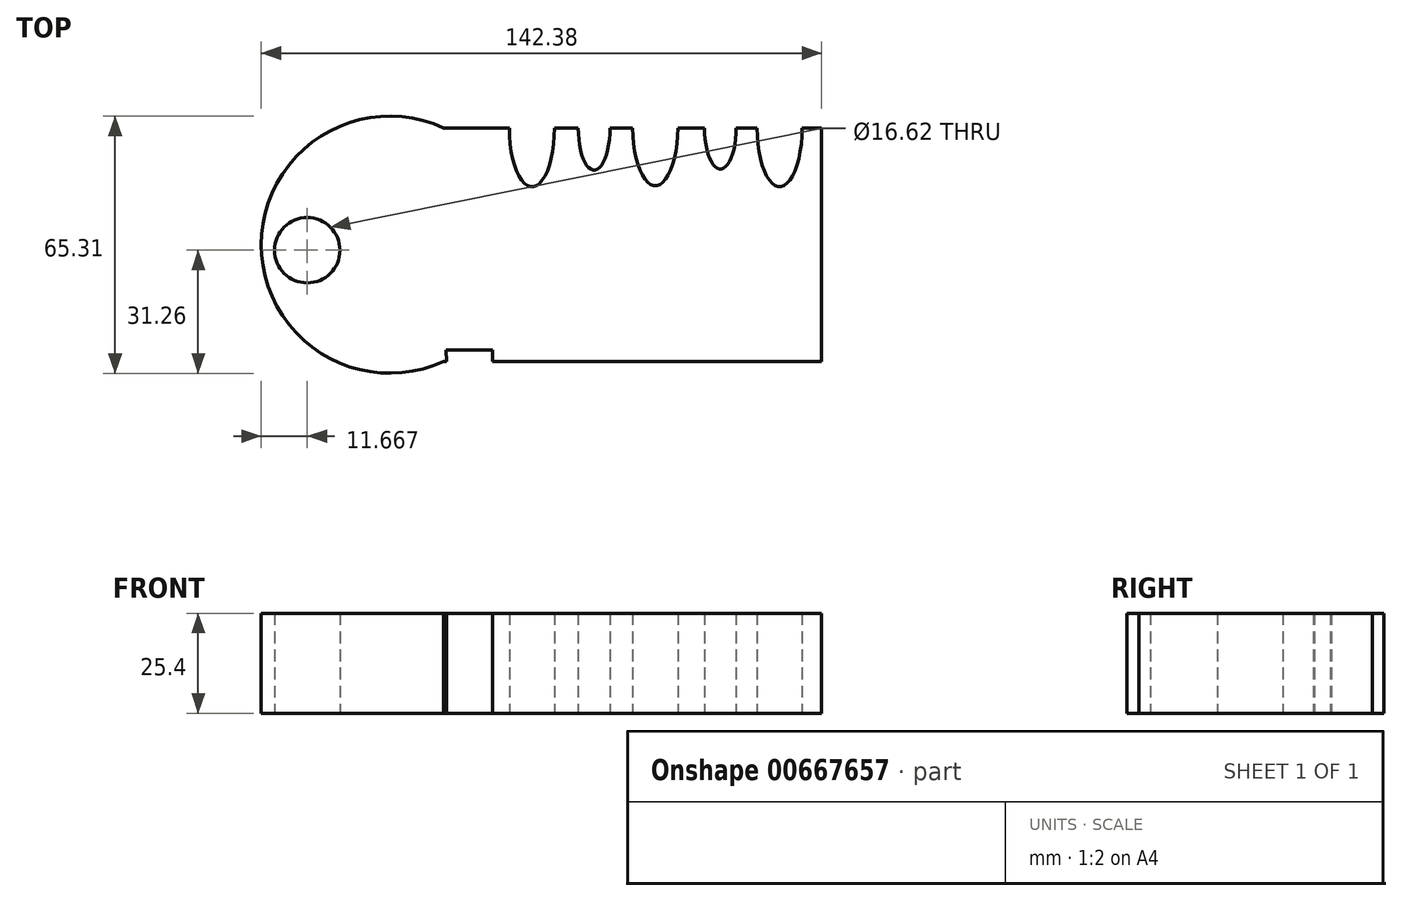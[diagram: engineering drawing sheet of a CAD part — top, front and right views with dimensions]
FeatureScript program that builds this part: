
annotation { "Feature Type Name" : "Feature", "Feature Type Description" : "" }
export const myFeature = defineFeature(function(context is Context, id is Id, definition is map)
    precondition{}
    {
        {
            var Q0;
            Q0=qCreatedBy(makeId("Top.planeOp"),FACE);
            var sketch = newSketch(context, id + "F0", { "sketchPlane" : qUnion([Q0])});
            skLineSegment(sketch, "E0.bottom", {"start": v(-24.54, 31.05) * mm, "end": v(71.52, 31.05) * mm});
            skLineSegment(sketch, "E0.top", {"start": v(-24.54, -28.26) * mm, "end": v(71.52, -28.26) * mm});
            skLineSegment(sketch, "E0.left", {"start": v(-24.54, 31.05) * mm, "end": v(-24.54, -28.26) * mm});
            skLineSegment(sketch, "E0.right", {"start": v(71.52, 31.05) * mm, "end": v(71.52, -28.26) * mm});
            skArc(sketch, "E1", {"start": v(-24.54, 31.05) * mm, "mid": v(-70.86, 1.4) * mm, "end": v(-24.54, -28.26) * mm});
            skSolve(sketch);
        }
        {
            var Q0;
            Q0=makeQuery(id+"F0.imprint","IMPRINT",FACE,{"disambiguationData":[TD([[makeQuery(id+"F0.imprint","IMPRINT",EDGE,{"derivedFrom":sQuery(id+"F0.wireOp",EDGE,"E0.bottom")}),-1.0]])]});
            var Q1;
            Q1=makeQuery(id+"F0.imprint","IMPRINT",FACE,{"disambiguationData":[TD([[makeQuery(id+"F0.imprint","IMPRINT",EDGE,{"derivedFrom":sQuery(id+"F0.wireOp",EDGE,"E0.left")}),-1.0]])]});
            extrude(context, id + "F1", {"entities" : qUnion([Q0, Q1]), "depth" : 25.4 * mm, "offsetDistance" : 25.4 * mm});
        }
        {
            var Q0;
            Q0=qCreatedBy(makeId("Top.planeOp"),FACE);
            var sketch = newSketch(context, id + "F2", { "sketchPlane" : qUnion([Q0])});
            skCircle(sketch, "E2", {"center": v(-53.84, 0) * mm, "radius": 6.97 * mm});
            skSolve(sketch);
        }
        {
            var Q0;
            Q0=makeQuery(id+"F2.imprint","IMPRINT",FACE,{"disambiguationData":[TD([[makeQuery(id+"F2.imprint","IMPRINT",EDGE,{"derivedFrom":sQuery(id+"F2.wireOp",EDGE,"E2")}),1.0]])]});
            extrude(context, id + "F3", {"entities" : qUnion([Q0]), "operationType" : NewBodyOperationType.ADD, "depth" : 25.4 * mm, "offsetDistance" : 25.4 * mm});
        }
        {
            var Q0;
            Q0=qCreatedBy(makeId("Top.planeOp"),FACE);
            var sketch = newSketch(context, id + "F4", { "sketchPlane" : qUnion([Q0])});
            skCircle(sketch, "E3", {"center": v(-59.2, 0) * mm, "radius": 8.3 * mm});
            skSolve(sketch);
        }
        {
            var Q0;
            Q0=makeQuery(id+"F4.imprint","IMPRINT",FACE,{"disambiguationData":[TD([[makeQuery(id+"F4.imprint","IMPRINT",EDGE,{"derivedFrom":sQuery(id+"F4.wireOp",EDGE,"E3")}),1.0]])]});
            extrude(context, id + "F5", {"entities" : qUnion([Q0]), "operationType" : NewBodyOperationType.REMOVE, "depth" : 43.69 * mm, "offsetDistance" : 25.4 * mm});
        }
        {
            var Q0;
            Q0=qCreatedBy(makeId("Top.planeOp"),FACE);
            var sketch = newSketch(context, id + "F6", { "sketchPlane" : qUnion([Q0])});
            skEllipse(sketch, "E4", {"center": v(-2.1, 31.14) * mm, "majorRadius": 15.05 * mm, "minorRadius": 5.74 * mm, "majorAxis": v(0, 1)});
            skEllipse(sketch, "E5", {"center": v(13.69, 30.9) * mm, "majorRadius": 10.54 * mm, "minorRadius": 4.02 * mm, "majorAxis": v(0, 1)});
            skEllipse(sketch, "E6", {"center": v(29.23, 31.44) * mm, "majorRadius": 15.05 * mm, "minorRadius": 5.74 * mm, "majorAxis": v(0, 1)});
            skEllipse(sketch, "E7", {"center": v(45.78, 31.2) * mm, "majorRadius": 10.54 * mm, "minorRadius": 4.02 * mm, "majorAxis": v(0, 1)});
            skEllipse(sketch, "E8", {"center": v(60.82, 31.23) * mm, "majorRadius": 15.05 * mm, "minorRadius": 5.74 * mm, "majorAxis": v(0, 1)});
            skSolve(sketch);
        }
        {
            var Q0;
            Q0=makeQuery(id+"F6.imprint","IMPRINT",FACE,{"disambiguationData":[TD([[makeQuery(id+"F6.imprint","IMPRINT",EDGE,{"derivedFrom":sQuery(id+"F6.wireOp",EDGE,"E4")}),1.0]])]});
            var Q1;
            Q1=makeQuery(id+"F6.imprint","IMPRINT",FACE,{"disambiguationData":[TD([[makeQuery(id+"F6.imprint","IMPRINT",EDGE,{"derivedFrom":sQuery(id+"F6.wireOp",EDGE,"E5")}),1.0]])]});
            var Q2;
            Q2=makeQuery(id+"F6.imprint","IMPRINT",FACE,{"disambiguationData":[TD([[makeQuery(id+"F6.imprint","IMPRINT",EDGE,{"derivedFrom":sQuery(id+"F6.wireOp",EDGE,"E6")}),1.0]])]});
            var Q3;
            Q3=makeQuery(id+"F6.imprint","IMPRINT",FACE,{"disambiguationData":[TD([[makeQuery(id+"F6.imprint","IMPRINT",EDGE,{"derivedFrom":sQuery(id+"F6.wireOp",EDGE,"E7")}),1.0]])]});
            var Q4;
            Q4=makeQuery(id+"F6.imprint","IMPRINT",FACE,{"disambiguationData":[TD([[makeQuery(id+"F6.imprint","IMPRINT",EDGE,{"derivedFrom":sQuery(id+"F6.wireOp",EDGE,"E8")}),1.0]])]});
            extrude(context, id + "F7", {"entities" : qUnion([Q0, Q1, Q2, Q3, Q4]), "operationType" : NewBodyOperationType.REMOVE, "depth" : 28.7 * mm, "offsetDistance" : 25.4 * mm});
        }
        {
            var Q0;
            Q0=qCreatedBy(makeId("Top.planeOp"),FACE);
            var sketch = newSketch(context, id + "F8", { "sketchPlane" : qUnion([Q0])});
            skLineSegment(sketch, "E9", {"start": v(-17.4, -22.29) * mm, "end": v(71.75, -22.29) * mm});
            skLineSegment(sketch, "E10", {"start": v(-17.4, -22.29) * mm, "end": v(-17.4, -27.3) * mm});
            skLineSegment(sketch, "E11", {"start": v(-17.4, -27.3) * mm, "end": v(-24.17, -27.3) * mm});
            skLineSegment(sketch, "E12", {"start": v(-24.17, -27.3) * mm, "end": v(-27.17, -29.3) * mm});
            skLineSegment(sketch, "E13", {"start": v(71.75, -33.56) * mm, "end": v(71.75, -22.29) * mm});
            skLineSegment(sketch, "E14", {"start": v(71.75, -33.56) * mm, "end": v(-17.4, -33.56) * mm});
            skLineSegment(sketch, "E15", {"start": v(-17.4, -22.29) * mm, "end": v(-17.4, -33.56) * mm});
            skSolve(sketch);
        }
        {
            var Q0;
            {var subQ1=sQuery(id+"F8.wireOp",EDGE,"E9");Q0=makeQuery(id+"F8.imprint","IMPRINT",FACE,{"disambiguationData":[TD([[makeQuery(id+"F8.imprint","IMPRINT",EDGE,{"derivedFrom":subQ1}),-1.0]])]});}
            extrude(context, id + "F9", {"entities" : qUnion([Q0]), "operationType" : NewBodyOperationType.REMOVE, "oppositeDirection" : true, "depth" : 25.4 * mm, "offsetDistance" : 25.4 * mm});
        }
        {
            var Q0;
            Q0=qCreatedBy(makeId("Top.planeOp"),FACE);
            var sketch = newSketch(context, id + "F10", { "sketchPlane" : qUnion([Q0])});
            skLineSegment(sketch, "E16", {"start": v(-23.66, -28.55) * mm, "end": v(-23.66, -35.56) * mm});
            skLineSegment(sketch, "E17", {"start": v(-23.66, -35.56) * mm, "end": v(-12.15, -35.56) * mm});
            skLineSegment(sketch, "E18", {"start": v(-12.15, -35.56) * mm, "end": v(-12.15, -25.3) * mm});
            skLineSegment(sketch, "E19", {"start": v(-12.15, -25.3) * mm, "end": v(-23.92, -25.3) * mm});
            skLineSegment(sketch, "E20", {"start": v(-23.92, -25.3) * mm, "end": v(-23.66, -35.56) * mm});
            skSolve(sketch);
        }
        {
            var Q0;
            Q0=makeQuery(id+"F10.imprint","IMPRINT",FACE,{"disambiguationData":[TD([[makeQuery(id+"F10.imprint","IMPRINT",EDGE,{"derivedFrom":sQuery(id+"F10.wireOp",EDGE,"E17")}),1.0]])]});
            extrude(context, id + "F11", {"entities" : qUnion([Q0]), "operationType" : NewBodyOperationType.REMOVE, "depth" : 36.83 * mm, "offsetDistance" : 25.4 * mm});
        }
    });
